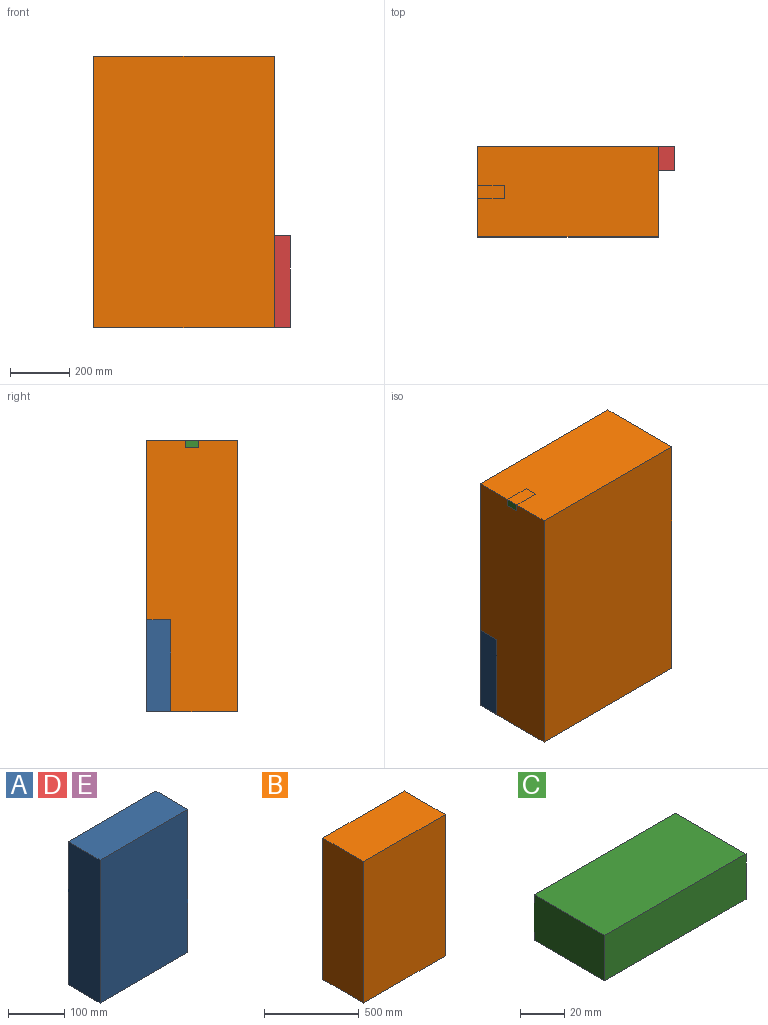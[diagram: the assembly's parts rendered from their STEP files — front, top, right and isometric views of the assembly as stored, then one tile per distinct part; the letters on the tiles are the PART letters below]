
ASSEMBLY  parts=5 mates=5
PART A: 6 faces, bbox 220x80x310 mm
  f0: plane 310x220mm, normal (0,1,0), area 68200mm2, adj f1,f3,f4,f5
  f1: plane 310x80mm, normal (-1,0,0), area 24800mm2, adj f0,f2,f4,f5
  f2: plane 310x220mm, normal (0,-1,0), area 68200mm2, adj f1,f3,f4,f5
  f3: plane 310x80mm, normal (1,0,0), area 24800mm2, adj f0,f2,f4,f5
  f4: plane 220x80mm, normal (0,0,1), area 17600mm2, adj f0,f1,f2,f3
  f5: plane 220x80mm, normal (0,0,-1), area 17600mm2, adj f0,f1,f2,f3
PART B: 6 faces, bbox 610x305x915 mm
  f0: plane 915x610mm, normal (0,1,0), area 558150mm2, adj f1,f3,f4,f5
  f1: plane 915x305mm, normal (-1,0,0), area 279075mm2, adj f0,f2,f4,f5
  f2: plane 915x610mm, normal (0,-1,0), area 558150mm2, adj f1,f3,f4,f5
  f3: plane 915x305mm, normal (1,0,0), area 279075mm2, adj f0,f2,f4,f5
  f4: plane 610x305mm, normal (0,0,1), area 186050mm2, adj f0,f1,f2,f3
  f5: plane 610x305mm, normal (0,0,-1), area 186050mm2, adj f0,f1,f2,f3
PART C: 6 faces, bbox 90x45x25 mm
  f0: plane 90x25mm, normal (0,1,0), area 2250mm2, adj f1,f3,f4,f5
  f1: plane 45x25mm, normal (-1,0,0), area 1125mm2, adj f0,f2,f4,f5
  f2: plane 90x25mm, normal (0,-1,0), area 2250mm2, adj f1,f3,f4,f5
  f3: plane 45x25mm, normal (1,0,0), area 1125mm2, adj f0,f2,f4,f5
  f4: plane 90x45mm, normal (0,0,1), area 4050mm2, adj f0,f1,f2,f3
  f5: plane 90x45mm, normal (0,0,-1), area 4050mm2, adj f0,f1,f2,f3
PART D: same geometry as A
PART E: same geometry as A
PLACE A t=(-443.33,-307.67,634.79)mm
PLACE B t=(-190.49,-392.02,634.79)mm
PLACE C rot(axis=(1,0,0),180deg) t=(-339,-459,1549.79)mm
PLACE D t=(0.67,-307.67,634.79)mm
PLACE E t=(-221.33,-307.67,634.79)mm
MATE planar A.f5 <-> B.f5  axis (0,0,-1) through (-375.91,-309.52,634.79)mm
MATE planar A.f1 <-> B.f1  axis (-1,0,0) through (-485.91,-309.52,789.79)mm
MATE planar A.f0 <-> B.f0  axis (0,1,0) through (-375.91,-269.52,789.79)mm
MATE planar C.f5 <-> B.f4  axis (0,0,1) through (-440.91,-422.02,1549.79)mm
MATE planar B.f1 <-> C.f1  axis (-1,0,0) through (-485.91,-422.02,1092.29)mm
